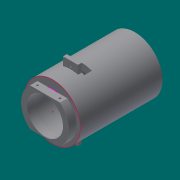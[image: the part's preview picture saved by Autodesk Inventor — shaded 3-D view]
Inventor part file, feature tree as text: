
AUTODESK INVENTOR PART (.ipt)
format: ipt  version: 2013 (Build 170138000, 138)  size: 215,040 bytes
history: native  units: mm
features: sketch x8, extrude x6, other x3, revolve x1, mirror x1
ambient origin geometry x8: Origin, YZ Plane, XZ Plane, XY Plane, X Axis, Y Axis, Z Axis, Center Point
feature tree (19):
  other  "ソリッド1"
  revolve  "回転1"
  other  "作業平面4"
  sketch  "スケッチ2"
  sketch  "スケッチ3"
  extrude  "押し出し1"  Depth=32.0mm
  extrude  "押し出し2"  Depth=30.0mm
  extrude  "押し出し3"  Depth=35.0mm
  extrude  "押し出し4"  Depth=2.0mm
  extrude  "押し出し5"  Depth=80.0mm
  mirror  "ミラー1"
  other  "作業平面5"
  extrude  "押し出し7"  TaperAngle=90.0deg  [1 undecoded]
  sketch  "スケッチ1"
  sketch  "スケッチ4"
  sketch  "スケッチ5"
  sketch  "スケッチ6"
  sketch  "スケッチ7"
  sketch  "スケッチ8"
note: 1 required parameter value undecoded (feature->parameter linkage not recoverable at this tier; creation-order binding heuristic only, values carry confidence <= 0.55)
